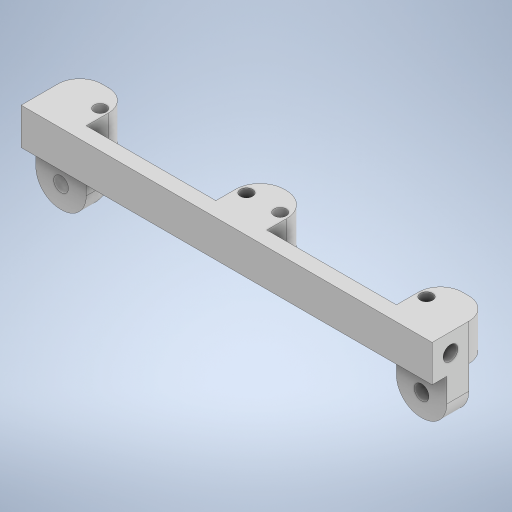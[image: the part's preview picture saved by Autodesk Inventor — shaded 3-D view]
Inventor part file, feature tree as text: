
AUTODESK INVENTOR PART (.ipt)
format: ipt  version: 2023 (Build 270158000, 158)  size: 463,360 bytes
history: native  units: in
note: dims shown in document units (in); Inventor stores cm internally (conversion verified against a paired STEP export)
features: reference x17, other x14, sketch x12, extrude x12, projected_geometry x10, fillet x3
ambient origin geometry x8: Origin, YZ Plane, XZ Plane, XY Plane, X Axis, Y Axis, Z Axis, Center Point
bodies: Body1 (feature_tree)
feature tree (68):
  other  "Bryła1"
  sketch  "Szkic1"
  other  "Płaszczyzna konstrukcyjna1"
  extrude  "Wyciągnięcie proste1"  Depth=0.0394in
  sketch  "Szkic2"
  other  "Płaszczyzna konstrukcyjna2"
  extrude  "Wyciągnięcie proste2"  Depth=0.0394in
  extrude  "Wyciągnięcie proste3"  Depth=0.0394in
  other  "Edytuj bezpośrednio1"
  sketch  "Szkic4"
  other  "Płaszczyzna konstrukcyjna3"
  extrude  "Wyciągnięcie proste4"  Depth=0.3937in TaperAngle=0.0deg
  other  "Edytuj bezpośrednio2"
  extrude  "Wyciągnięcie proste5"  Depth=0.3937in TaperAngle=0.0deg
  extrude  "Wyciągnięcie proste6"  Depth=0.1969in TaperAngle=0.0deg
  extrude  "Wyciągnięcie proste7"  TaperAngle=0.0deg  [1 undecoded]
  extrude  "Wyciągnięcie proste8"  Depth=0.1969in TaperAngle=0.0deg
  fillet  "Zaokrąglenie1"  [1 undecoded]
  fillet  "Zaokrąglenie2"  Radius=0.1181in
  fillet  "Zaokrąglenie3"  [1 undecoded]
  extrude  "Wyciągnięcie proste9"  Depth=0.3937in TaperAngle=0.0deg
  extrude  "Wyciągnięcie proste10"  TaperAngle=0.0deg  [1 undecoded]
  extrude  "Wyciągnięcie proste11"  Depth=0.0591in
  extrude  "Wyciągnięcie proste12"  Depth=0.1181in
  reference  "Odniesienie1"
  reference  "Odniesienie2"
  reference  "Odniesienie3"
  reference  "Odniesienie4"
  reference  "Odniesienie5"
  reference  "Odniesienie6"
  reference  "Odniesienie7"
  reference  "Odniesienie8"
  reference  "Odniesienie9"
  reference  "Odniesienie10"
  reference  "Odniesienie11"
  projected_geometry  "Pętla rzutowana1"
  projected_geometry  "Pętla rzutowana2"
  projected_geometry  "Pętla rzutowana3"
  sketch  "Szkic3"
  projected_geometry  "Pętla rzutowana4"
  reference  "Odniesienie12"
  sketch  "Szkic5"
  sketch  "Szkic6"
  projected_geometry  "Pętla rzutowana5"
  sketch  "Szkic7"
  projected_geometry  "Pętla rzutowana6"
  sketch  "Szkic8"
  projected_geometry  "Pętla rzutowana7"
  projected_geometry  "Pętla rzutowana8"
  sketch  "Szkic9"
  projected_geometry  "Pętla rzutowana9"
  reference  "Odniesienie13"
  reference  "Odniesienie14"
  reference  "Odniesienie15"
  reference  "Odniesienie16"
  sketch  "Szkic10"
  reference  "Odniesienie17"
  sketch  "Szkic11"
  projected_geometry  "Pętla rzutowana10"
  sketch  "Szkic12"
  other  "servo_stefan_MIR:1"
  other  "servo_stefan:1"
  other  "SCIANA_2.0_MIR:1"
  other  "SCIANA_2.0:1"
  other  "opona_nowa:1"
  other  "Przesuń1"
  other  "bateria szczurza:1"
  other  "Przesuń2"
note: 4 required parameter values undecoded (feature->parameter linkage not recoverable at this tier; creation-order binding heuristic only, values carry confidence <= 0.55)
